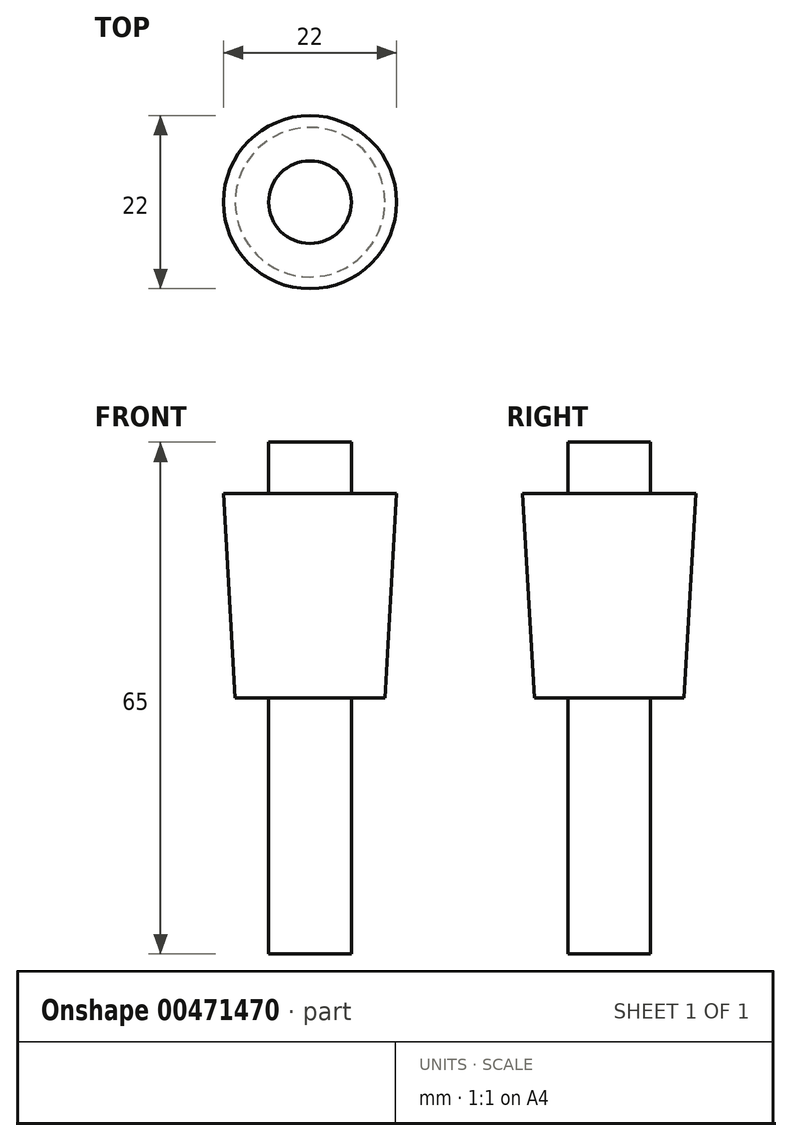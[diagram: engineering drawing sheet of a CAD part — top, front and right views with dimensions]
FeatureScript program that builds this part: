
annotation { "Feature Type Name" : "Feature", "Feature Type Description" : "" }
export const myFeature = defineFeature(function(context is Context, id is Id, definition is map)
    precondition{}
    {
        {
            var Q0;
            Q0=qCreatedBy(makeId("Top.planeOp"),FACE);
            var sketch = newSketch(context, id + "F0", { "sketchPlane" : qUnion([Q0])});
            skCircle(sketch, "E0", {"center": v(0, 0) * mm, "radius": 9.5 * mm});
            skSolve(sketch);
        }
        {
            var Q0;
            Q0=qCreatedBy(makeId("Top.planeOp"),FACE);
            cPlane(context, id + "F1", {"entities" : qUnion([Q0]), "cplaneType" : CPlaneType.OFFSET, "offset" : 26 * mm, "width" : 150 * mm, "height" : 150 * mm});
        }
        {
            var Q0;
            Q0=qCreatedBy(id+"F1.planeOp",FACE);
            var sketch = newSketch(context, id + "F2", { "sketchPlane" : qUnion([Q0])});
            skCircle(sketch, "E1", {"center": v(0, 0) * mm, "radius": 11 * mm});
            skSolve(sketch);
        }
        {
            var Q0;
            Q0=makeQuery(id+"F2.imprint","IMPRINT",FACE,{"disambiguationData":[TD([[makeQuery(id+"F2.imprint","IMPRINT",EDGE,{"derivedFrom":sQuery(id+"F2.wireOp",EDGE,"E1")}),1.0]])]});
            var Q1;
            Q1=makeQuery(id+"F0.imprint","IMPRINT",FACE,{"disambiguationData":[TD([[makeQuery(id+"F0.imprint","IMPRINT",EDGE,{"derivedFrom":sQuery(id+"F0.wireOp",EDGE,"E0")}),1.0]])]});
            loft(context, id + "F3", {"sheetProfilesArray" : [{ "sheetProfileEntities" : qUnion([Q0]) }, { "sheetProfileEntities" : qUnion([Q1]) }]});
        }
        {
            var Q0;
            Q0=qCreatedBy(makeId("Top.planeOp"),FACE);
            var sketch = newSketch(context, id + "F4", { "sketchPlane" : qUnion([Q0])});
            skCircle(sketch, "E2", {"center": v(0, 0) * mm, "radius": 5.25 * mm});
            skSolve(sketch);
        }
        {
            var Q0;
            Q0 = qSketchRegion(id + "F4", true);
            extrude(context, id + "F5", {"entities" : qUnion([Q0]), "operationType" : NewBodyOperationType.ADD, "endBound" : BoundingType.SYMMETRIC, "depth" : 65 * mm});
        }
    });
